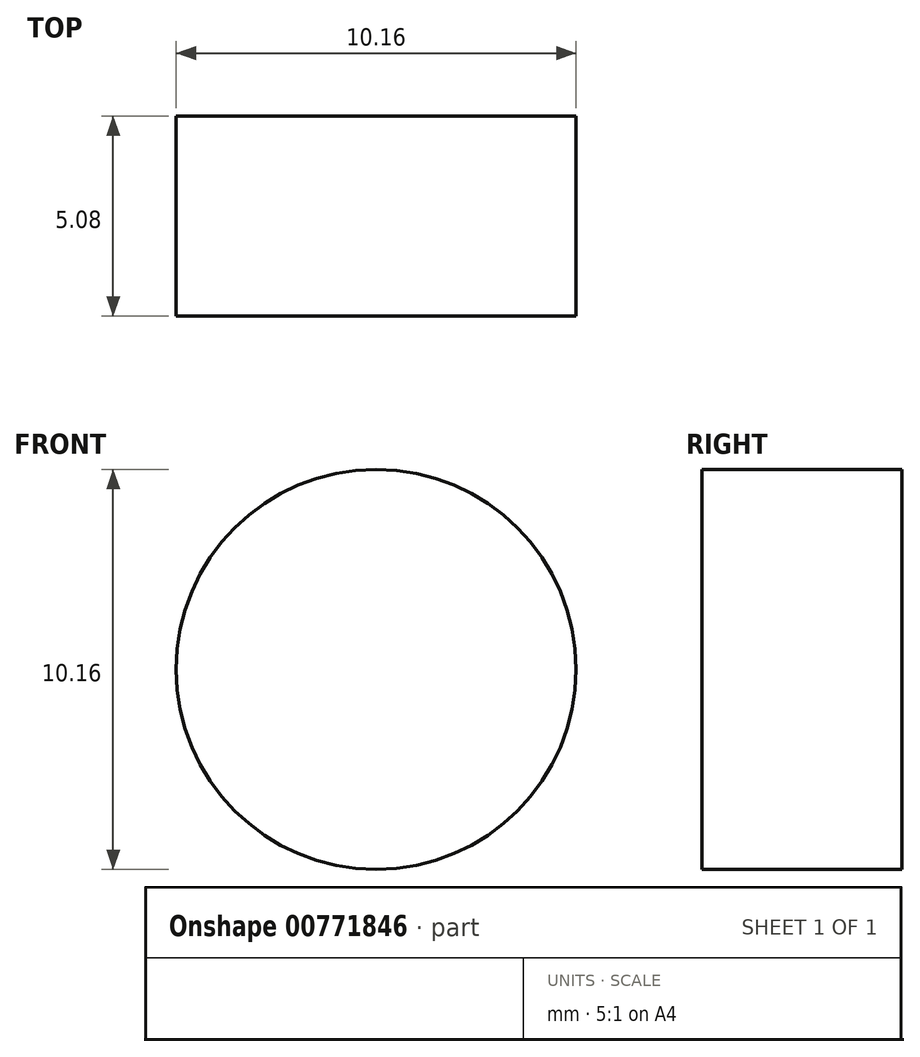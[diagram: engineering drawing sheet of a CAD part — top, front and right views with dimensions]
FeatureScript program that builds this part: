
annotation { "Feature Type Name" : "Feature", "Feature Type Description" : "" }
export const myFeature = defineFeature(function(context is Context, id is Id, definition is map)
    precondition{}
    {
        {
            var Q0;
            Q0=qCreatedBy(makeId("Front.planeOp"),FACE);
            var sketch = newSketch(context, id + "F0", { "sketchPlane" : qUnion([Q0])});
            skCircle(sketch, "E0", {"center": v(-38.48, 13.84) * mm, "radius": 5.08 * mm});
            skSolve(sketch);
        }
        {
            var Q0;
            Q0 = qSketchRegion(id + "F0", true);
            extrude(context, id + "F1", {"entities" : qUnion([Q0]), "depth" : 5.08 * mm, "offsetDistance" : 25.4 * mm});
        }
    });
